# Revit family: NaughtOne_HatchThreeSeatLounge
name_source: partatom
category: Furniture
units: mm (PartAtom-declared; Revit-internal decimal feet)

## family parameters
Always vertical = Yes
Cut with Voids When Loaded = No
Enable Cutting in Views = No
Render Appearance Source = Family Geometry
Room Calculation Point = No
Shared = Yes
Work Plane-Based = No

## types (8) — shared parameters
Assembly Code = E2020200
AssetType = Moveable
BIMObjectName = Naughtone_Seating_Hatch
Category = Pr_40_50_12: Chairs, seats and benches
CodePerformance = PASSED BSEN 16139
Color = Various
DurationUnit = year
Export Type to IFC As = IfcFurnishingElementType
Finish = Upholstered
IfcExportAs = IfcFurnishingElementType
IfcExportType = SOFA
Is2Seat = Yes
Is3Seat = Yes
IsChair = No
Keynote = Pr_40_50_12
LeftOffset = 765 mm  [stored 2.50984 ft]
MainColor = Various
Manufacturer = naughtone
ManufacturerAddressUK = naughtone, Knaresborough Tech Park, Manse Lane, Knaresborough, HG5 8LF
ManufacturerName = Naughtone
ManufacturerURL = www.naughtone.com
Material = Fabric, leather/steel/solid wood/beech ply/foam
ModelNumber = HAT3RA
ModelReference = Hatch 3 Seater Right Arm
NBSDescription = Seating
NBSReference = 45-35-72/352
Name = Seating_Hatch_Naughtone
NominalHeight = 685 mm  [stored 2.24738 ft]
NominalWidth = 690 mm  [stored 2.26378 ft]
Package Qty = 1
Product Documentation Link = http://www.naughtone.com
ProductInformation = www.naughtone.com/portfolio-view/hatch
RightOffset = 765 mm  [stored 2.50984 ft]
Shape = Rectangular
Size = 1710x690x685mm
SustainabilityPerformance = FSC certified. FISP certified. ISO 14001 certified
Type IFC Predefined Type = SOFA
URL = http://www.hermanmiller.com
Uniclass2015Description = Chairs, seats and benches
Uniclass2015Reference = Pr_40_50_12
Uniclass2015Version = Products v1.5
Version = 1
VoidOffsetCentre = 255 mm  [stored 0.836614 ft]
WarrantyDurationLabor = 5
WarrantyDurationParts = 5
WarrantyDurationUnit = year
zero-valued in all types: Default Elevation, VoidOffset2Seat, VoidOffset3Seat

## per-type parameters (varying)
| type | Description | HasNoArms | HasOneArmL | HasOneArmR | HasTwoArms | Model |
| HAT3NA Single Lounge Ht | Hatch Three Seat No Arms lounge height 16 inch seat height Single Fabric | Yes | No | No | No | NOHAN320L1 |
| HATNA Multiple Lounge Ht | Hatch Three Seat No Arms lounge height 16 inch seat height Multiple Fabric | Yes | No | No | No | NOHAN320L2 |
| HAT3RA Single Lounge Ht | Hatch Three Seat Right Arm lounge height 16 inch seat height Single Fabric | No | No | Yes | No | NOHAN330L1 |
| HAT3RA Multiple Lounge Ht | Hatch Three Seat Right Arm lounge height 16 inch seat height Multiple Fabric | No | No | Yes | No | NOHAN330L2 |
| HAT3LA Single Lounge Ht | Hatch Three Seat Left Arm lounge height 16 inch seat height Single Fabric | No | Yes | No | No | NOHAN340L1 |
| HAT3LA Multiple Lounge Ht | Hatch Three Seat Left Arm lounge height 16 inch seat height Multiple Fabric | No | Yes | No | No | NOHAN340L2 |
| HAT32A Single Lounge Ht | Hatch Three Seat Two Arms lounge height 16 inch seat height Single Fabric | No | No | No | Yes | NOHAN350L1 |
| HAT32A Multiple Lounge Ht | Hatch Three Seat Two Arms lounge height 16 inch seat height Multiple Fabric | No | No | No | Yes | NOHAN350L2 |

note: [stored X ft] marks values corroborated as IEEE doubles in the binary element streams (Revit-internal decimal feet)

## geometry (parser evidence)
native form markers: Sweep x4
no freeform markers — native parametric forms only
